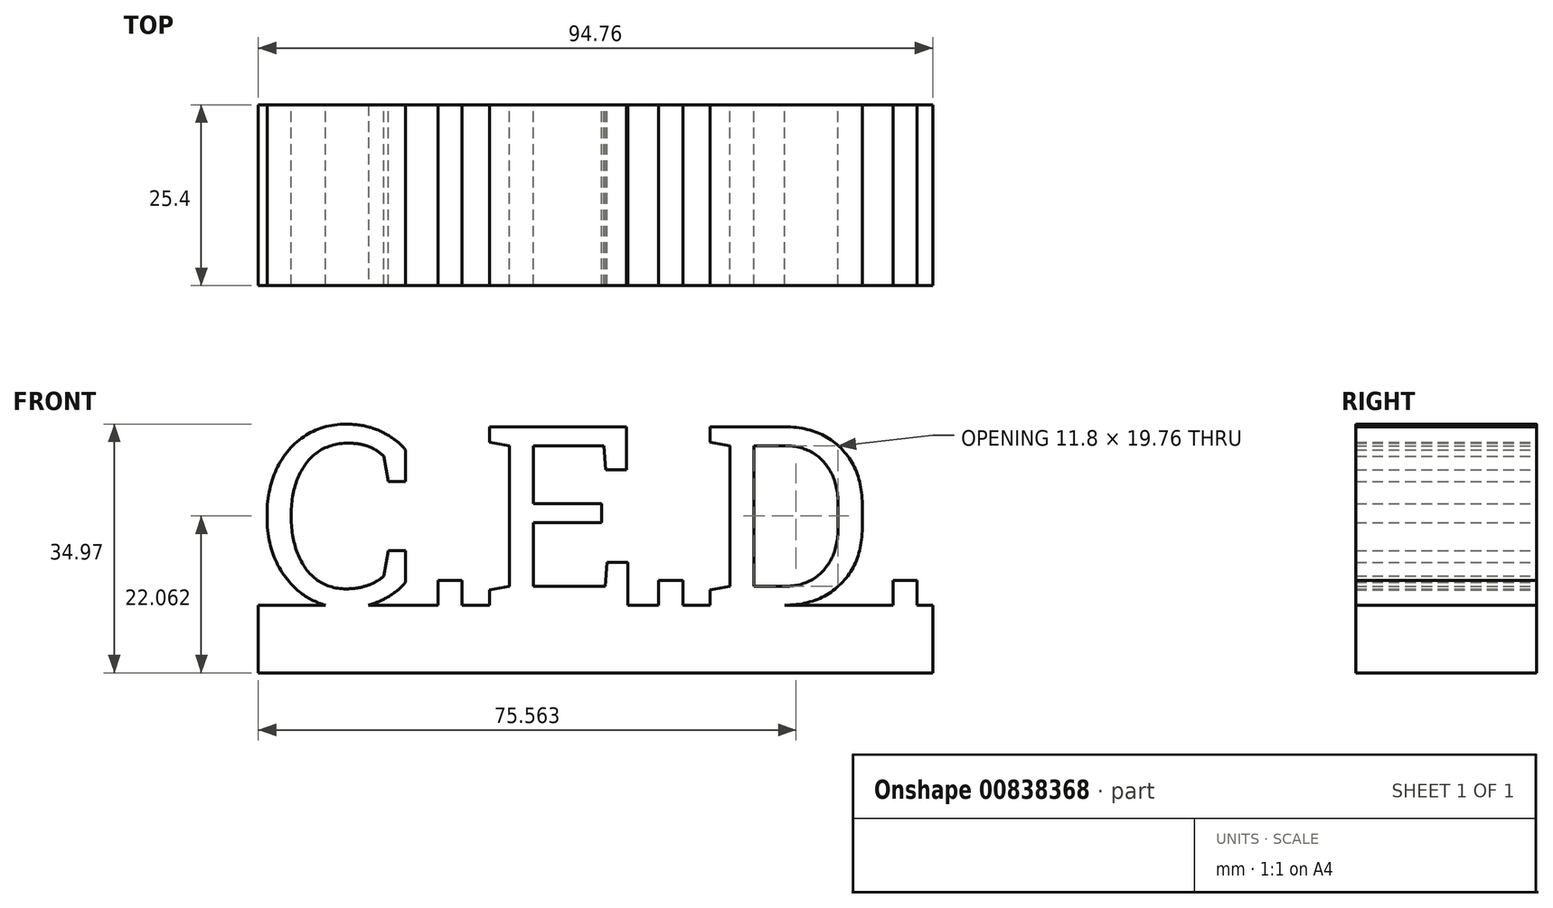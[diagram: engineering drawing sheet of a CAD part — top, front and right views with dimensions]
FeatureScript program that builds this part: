
annotation { "Feature Type Name" : "Feature", "Feature Type Description" : "" }
export const myFeature = defineFeature(function(context is Context, id is Id, definition is map)
    precondition{}
    {
        {
            var Q0;
            Q0=qCreatedBy(makeId("Front.planeOp"),FACE);
            var sketch = newSketch(context, id + "F0", { "sketchPlane" : qUnion([Q0])});
            skText(sketch, "E0", { "text": "C.E.D.", "fontName": "RobotoSlab-Regular.ttf"});
            skLineSegment(sketch, "E1.bottom", {"start": v(-47.38, 0) * mm, "end": v(47.38, 0) * mm});
            skLineSegment(sketch, "E1.top", {"start": v(-47.38, -9.53) * mm, "end": v(47.38, -9.53) * mm});
            skLineSegment(sketch, "E1.left", {"start": v(-47.38, 0) * mm, "end": v(-47.38, -9.53) * mm});
            skLineSegment(sketch, "E1.right", {"start": v(47.38, 0) * mm, "end": v(47.38, -9.53) * mm});
            const initialGuessF0  = {"E0": [-0.04738, 0, 1, 0, 0.0254]};
            skSetInitialGuess(sketch, initialGuessF0);
            skSolve(sketch);
        }
        {
            var Q0;
            Q0 = qSketchRegion(id + "F0", true);
            extrude(context, id + "F1", {"entities" : qUnion([Q0]), "depth" : 25.4 * mm, "offsetDistance" : 25.4 * mm});
        }
    });
